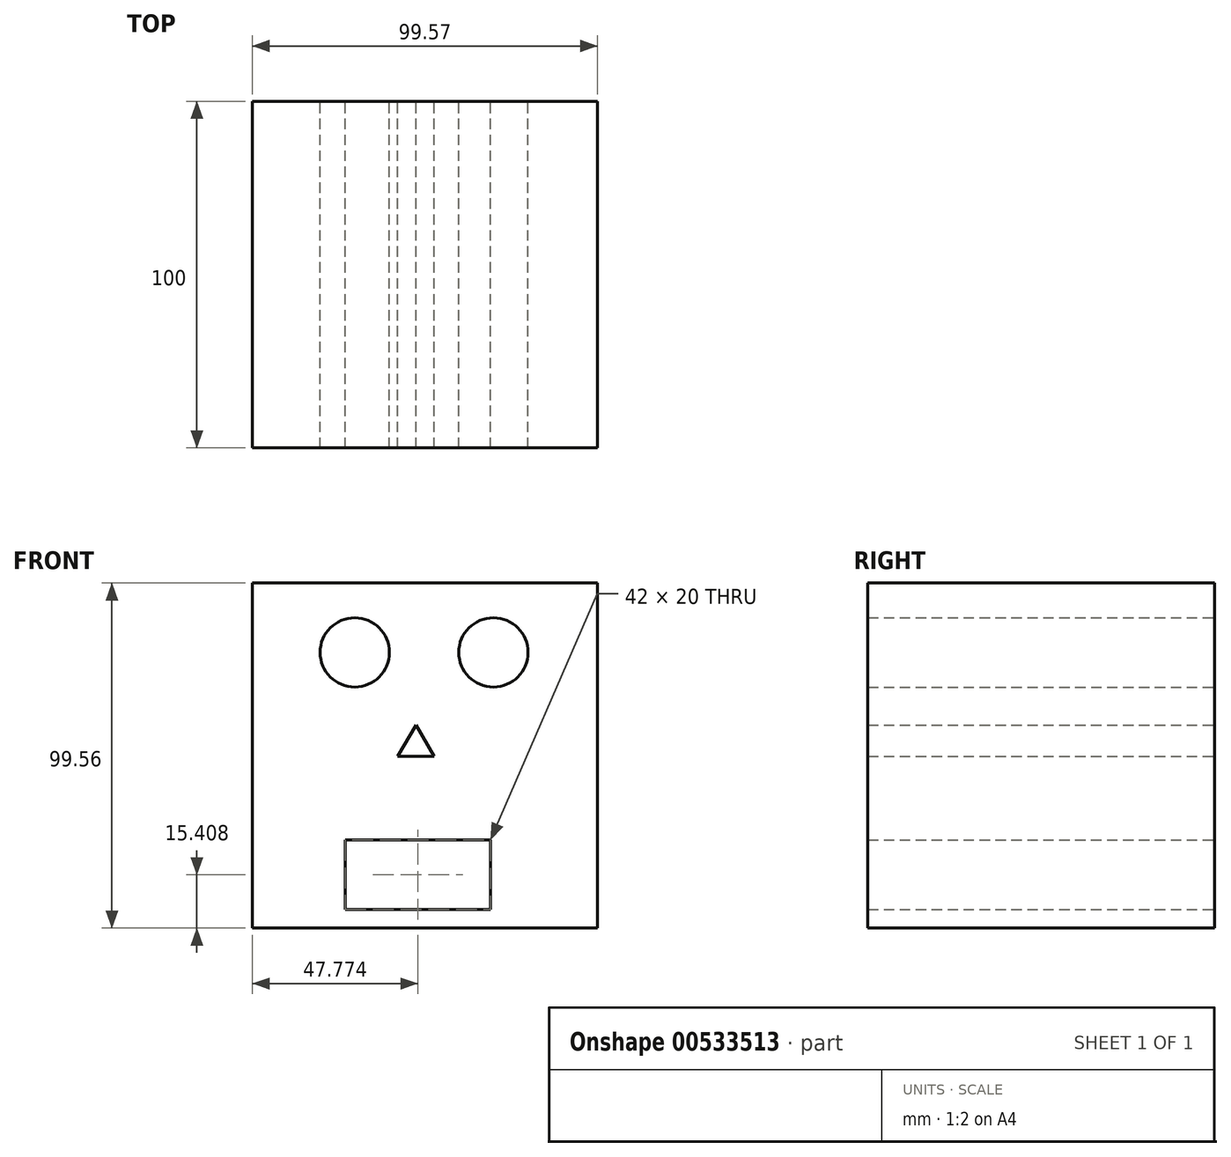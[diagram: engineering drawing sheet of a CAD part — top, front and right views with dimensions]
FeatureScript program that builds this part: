
annotation { "Feature Type Name" : "Feature", "Feature Type Description" : "" }
export const myFeature = defineFeature(function(context is Context, id is Id, definition is map)
    precondition{}
    {
        {
            var Q0;
            Q0=qCreatedBy(makeId("Front.planeOp"),FACE);
            var sketch = newSketch(context, id + "F0", { "sketchPlane" : qUnion([Q0])});
            skLineSegment(sketch, "E0.bottom", {"start": v(52.3, 50.02) * mm, "end": v(-47.7, 50.02) * mm});
            skLineSegment(sketch, "E0.top", {"start": v(52.3, -49.98) * mm, "end": v(-47.7, -49.98) * mm});
            skLineSegment(sketch, "E0.right", {"start": v(-47.7, 50.02) * mm, "end": v(-47.7, -49.98) * mm});
            skCircle(sketch, "E1", {"center": v(-17.7, 30.02) * mm, "radius": 10 * mm});
            skCircle(sketch, "E2", {"center": v(22.3, 30.02) * mm, "radius": 10 * mm});
            skLineSegment(sketch, "E3", {"start": v(-5.27, 0.02) * mm, "end": v(0, 9.1) * mm});
            skPoint(sketch, "E3.startSnap0", {"position": v(-47.7, 0.02) * mm});
            skLineSegment(sketch, "E4", {"start": v(0, 9.1) * mm, "end": v(5.23, 0) * mm});
            skLineSegment(sketch, "E5", {"start": v(-5.27, 0.02) * mm, "end": v(5.23, 0) * mm});
            skLineSegment(sketch, "E6.bottom", {"start": v(-20.49, -24.13) * mm, "end": v(21.51, -24.13) * mm});
            skLineSegment(sketch, "E6.top", {"start": v(-20.49, -44.13) * mm, "end": v(21.51, -44.13) * mm});
            skLineSegment(sketch, "E6.left", {"start": v(-20.49, -24.13) * mm, "end": v(-20.49, -44.13) * mm});
            skLineSegment(sketch, "E6.right", {"start": v(21.51, -24.13) * mm, "end": v(21.51, -44.13) * mm});
            skLineSegment(sketch, "E7.bottom", {"start": v(51.64, 49.65) * mm, "end": v(-47.26, 49.65) * mm});
            skLineSegment(sketch, "E7.top", {"start": v(51.64, -49.54) * mm, "end": v(-47.26, -49.54) * mm});
            skLineSegment(sketch, "E7.left", {"start": v(51.64, 49.65) * mm, "end": v(51.64, -49.54) * mm});
            skLineSegment(sketch, "E7.right", {"start": v(-47.26, 49.65) * mm, "end": v(-47.26, -49.54) * mm});
            skLineSegment(sketch, "E8.bottom", {"start": v(52.3, 50.02) * mm, "end": v(-47.26, 50.02) * mm});
            skLineSegment(sketch, "E8.top", {"start": v(52.3, -49.54) * mm, "end": v(-47.26, -49.54) * mm});
            skLineSegment(sketch, "E8.left", {"start": v(52.3, 50.02) * mm, "end": v(52.3, -49.54) * mm});
            skLineSegment(sketch, "E8.right", {"start": v(-47.26, 50.02) * mm, "end": v(-47.26, -49.54) * mm});
            skSolve(sketch);
        }
        {
            var Q0;
            Q0 = qSketchRegion(id + "F0", true);
            extrude(context, id + "F1", {"entities" : qUnion([Q0]), "depth" : 100 * mm, "offsetDistance" : 25 * mm});
        }
        {
            var Q0;
            Q0=makeQuery(id+"F1.opExtrude","CAP_FACE",FACE,{"disambiguationData":[OSD([sQuery(id+"F0.wireOp",EDGE,"E0.bottom"),sQuery(id+"F0.wireOp",EDGE,"E0.top"),sQuery(id+"F0.wireOp",EDGE,"E0.left"),sQuery(id+"F0.wireOp",EDGE,"E0.right"),sQuery(id+"F0.wireOp",EDGE,"E1"),sQuery(id+"F0.wireOp",EDGE,"E2"),sQuery(id+"F0.wireOp",EDGE,"E3"),sQuery(id+"F0.wireOp",EDGE,"E4"),sQuery(id+"F0.wireOp",EDGE,"E5"),sQuery(id+"F0.wireOp",EDGE,"E6.bottom"),sQuery(id+"F0.wireOp",EDGE,"E6.top"),sQuery(id+"F0.wireOp",EDGE,"E6.left"),sQuery(id+"F0.wireOp",EDGE,"E6.right")])],"isStart":true});
            var sketch = newSketch(context, id + "F2", { "sketchPlane" : qUnion([Q0])});
            skSolve(sketch);
        }
        {
            var Q0;
            Q0 = qSketchRegion(id + "F0", true);
            extrude(context, id + "F3", {"entities" : qUnion([Q0]), "operationType" : NewBodyOperationType.ADD, "depth" : 25 * mm, "offsetDistance" : 25 * mm});
        }
    });
